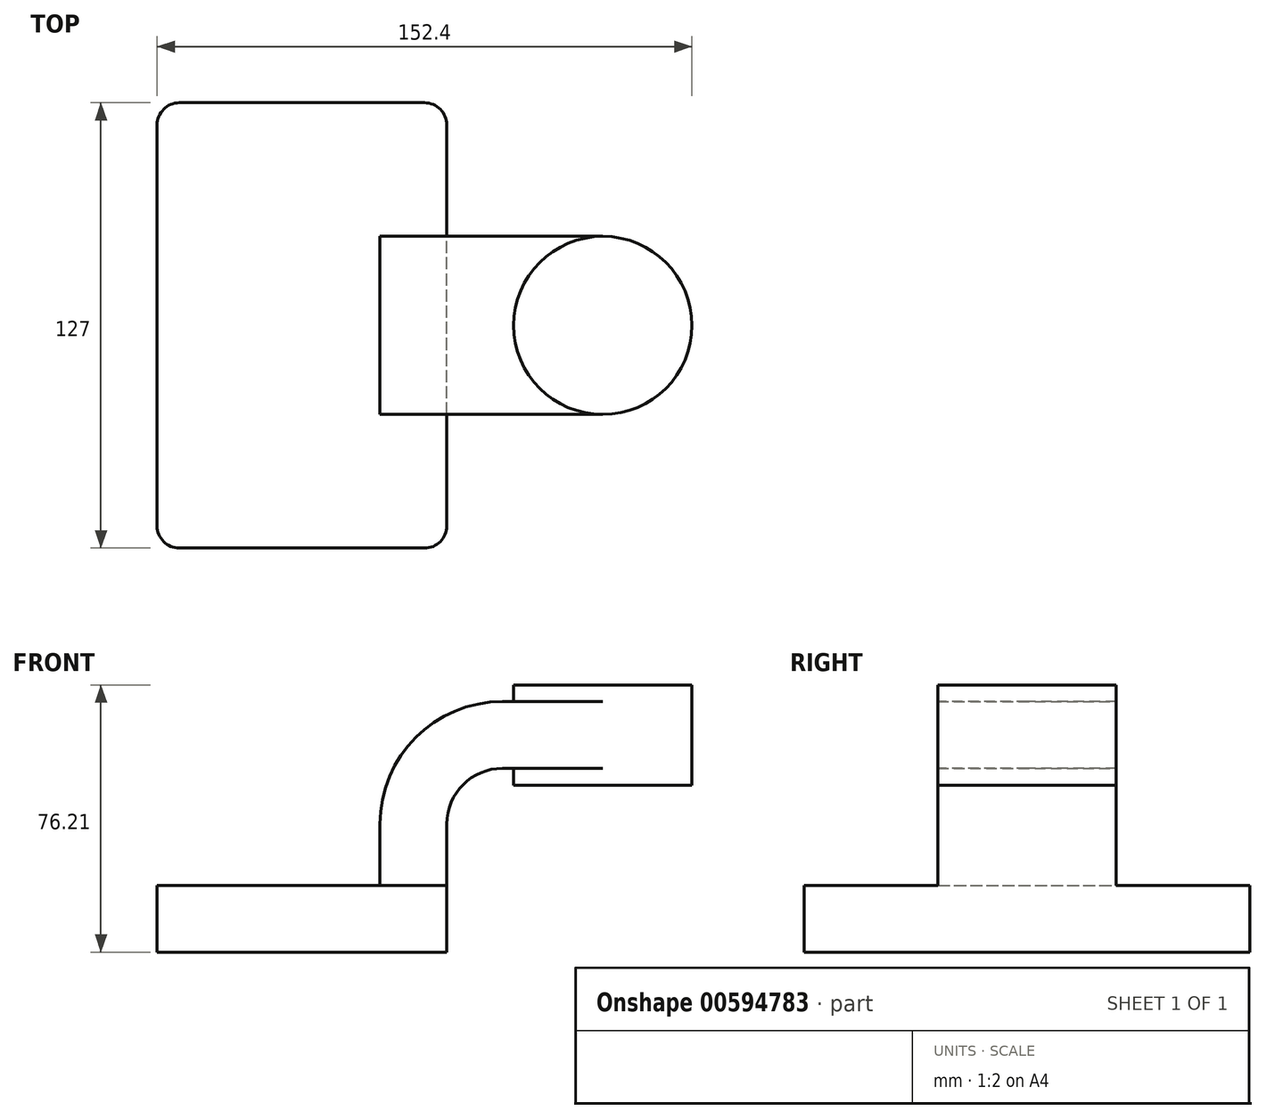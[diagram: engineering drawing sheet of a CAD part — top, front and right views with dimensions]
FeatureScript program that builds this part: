
annotation { "Feature Type Name" : "Feature", "Feature Type Description" : "" }
export const myFeature = defineFeature(function(context is Context, id is Id, definition is map)
    precondition{}
    {
        {
            var Q0;
            Q0=qCreatedBy(makeId("Front.planeOp"),FACE);
            var sketch = newSketch(context, id + "F0", { "sketchPlane" : qUnion([Q0])});
            skLineSegment(sketch, "E0.bottom", {"start": v(-41.28, 9.52) * mm, "end": v(41.27, 9.53) * mm});
            skLineSegment(sketch, "E0.top", {"start": v(-41.28, -9.53) * mm, "end": v(41.28, -9.53) * mm});
            skLineSegment(sketch, "E0.left", {"start": v(-41.28, 9.52) * mm, "end": v(-41.27, -9.53) * mm});
            skLineSegment(sketch, "E0.right", {"start": v(41.28, 9.53) * mm, "end": v(41.28, -9.52) * mm});
            skPoint(sketch, "E0.middle", {"position": v(0, 0) * mm});
            skLineSegment(sketch, "E1.bottom", {"start": v(60.32, 38.1) * mm, "end": v(111.12, 38.1) * mm});
            skLineSegment(sketch, "E1.top", {"start": v(60.32, 66.68) * mm, "end": v(111.12, 66.68) * mm});
            skLineSegment(sketch, "E1.left", {"start": v(60.32, 38.1) * mm, "end": v(60.32, 66.68) * mm});
            skLineSegment(sketch, "E1.right", {"start": v(111.12, 38.1) * mm, "end": v(111.12, 66.68) * mm});
            skPoint(sketch, "E1.middle", {"position": v(85.72, 52.39) * mm});
            skLineSegment(sketch, "E2", {"start": v(41.27, 9.53) * mm, "end": v(41.27, 27) * mm});
            skArc(sketch, "E3", {"start": v(41.27, 27) * mm, "mid": v(45.92, 38.23) * mm, "end": v(57.15, 42.88) * mm});
            skLineSegment(sketch, "E4", {"start": v(57.15, 42.88) * mm, "end": v(85.72, 42.88) * mm});
            skLineSegment(sketch, "E5.0", {"start": v(57.15, 61.93) * mm, "end": v(85.72, 61.93) * mm});
            skArc(sketch, "E5.1", {"start": v(22.22, 27) * mm, "mid": v(32.45, 51.7) * mm, "end": v(57.15, 61.93) * mm});
            skLineSegment(sketch, "E5.2", {"start": v(22.22, 9.53) * mm, "end": v(22.22, 27) * mm});
            skLineSegment(sketch, "E6", {"start": v(85.72, 42.88) * mm, "end": v(85.72, 66.68) * mm});
            skFitSpline(sketch, "E7", {"points": [v(-41.28, 9.52) * mm, v(57.15, 61.93) * mm], "startDerivative": vector(0.46, 138.36) * mm, "endDerivative": vector(113.63, 0) * mm});
            skLineSegment(sketch, "E8", {"start": v(85.72, 38.1) * mm, "end": v(85.72, 42.88) * mm});
            skSolve(sketch);
        }
        {
            var Q0;
            Q0=makeQuery(id+"F0.imprint","IMPRINT",FACE,{"disambiguationData":[TD([[makeQuery(id+"F0.imprint","IMPRINT",EDGE,{"derivedFrom":sQuery(id+"F0.wireOp",EDGE,"E0.top")}),1.0]])]});
            extrude(context, id + "F1", {"entities" : qUnion([Q0]), "depth" : 127 * mm, "offsetDistance" : 25.4 * mm, "symmetric" : true});
        }
        {
            var Q0;
            {var subQ1=sQuery(id+"F0.wireOp",EDGE,"E2");Q0=makeQuery(id+"F0.imprint","IMPRINT",FACE,{"disambiguationData":[TD([[makeQuery(id+"F0.imprint","IMPRINT",EDGE,{"derivedFrom":subQ1}),1.0]])]});}
            var Q1;
            {var subQ0=sQuery(id+"F0.wireOp",EDGE,"E4");var subQ1=sQuery(id+"F0.wireOp",EDGE,"E1.left");var subQ2=makeQuery(id+"F0.imprint","INTERSECT",VERTEX,{"derivedFrom":[subQ1,subQ0]});Q1=makeQuery(id+"F0.imprint","IMPRINT",FACE,{"disambiguationData":[TD([[makeQuery(id+"F0.imprint","IMPRINT",EDGE,{"disambiguationData":[TD([[subQ2,-1.0]])],"derivedFrom":subQ1}),-1.0]])]});}
            extrude(context, id + "F2", {"entities" : qUnion([Q0, Q1]), "operationType" : NewBodyOperationType.ADD, "depth" : 50.8 * mm, "offsetDistance" : 25.4 * mm, "symmetric" : true});
        }
        {
            var Q0;
            Q0=makeQuery(id+"F0.imprint","IMPRINT",FACE,{"disambiguationData":[TD([[makeQuery(id+"F0.imprint","IMPRINT",EDGE,{"derivedFrom":sQuery(id+"F0.wireOp",EDGE,"E5.1")}),1.0]])]});
            extrude(context, id + "F3", {"entities" : qUnion([Q0]), "operationType" : NewBodyOperationType.ADD, "depth" : 15.88 * mm, "offsetDistance" : 25.4 * mm, "symmetric" : true});
        }
        {
            var Q0;
            {var subQ0=sQuery(id+"F0.wireOp",EDGE,"E1.right");Q0=makeQuery(id+"F0.imprint","IMPRINT",FACE,{"disambiguationData":[TD([[makeQuery(id+"F0.imprint","IMPRINT",EDGE,{"derivedFrom":subQ0}),1.0]])]});}
            var Q1;
            Q1=sQuery(id+"F0.wireOp",EDGE,"E6");
            revolve(context, id + "F4", {"operationType" : NewBodyOperationType.ADD, "entities" : qUnion([Q0]), "axis" : qUnion([Q1]), "revolveType" : RevolveType.FULL});
        }
        {
            var Q0;
            Q0=makeQuery(id+"F1.opExtrude","CAP_EDGE",EDGE,{"disambiguationData":[OSD([sQuery(id+"F0.wireOp",EDGE,"E0.right")])],"isStart":false});
            var Q1;
            Q1=makeQuery(id+"F1.opExtrude","CAP_EDGE",EDGE,{"disambiguationData":[OSD([sQuery(id+"F0.wireOp",EDGE,"E0.right")])],"isStart":true});
            var Q2;
            Q2=makeQuery(id+"F1.opExtrude","CAP_EDGE",EDGE,{"disambiguationData":[OSD([sQuery(id+"F0.wireOp",EDGE,"E0.left")])],"isStart":true});
            var Q3;
            Q3=makeQuery(id+"F1.opExtrude","CAP_EDGE",EDGE,{"disambiguationData":[OSD([sQuery(id+"F0.wireOp",EDGE,"E0.left")])],"isStart":false});
            fillet(context, id + "F5", {"entities" : qUnion([Q0, Q1, Q2, Q3]), "radius" : 6.35 * mm, "tangentPropagation" : true, "allowEdgeOverflow" : false});
        }
    });
